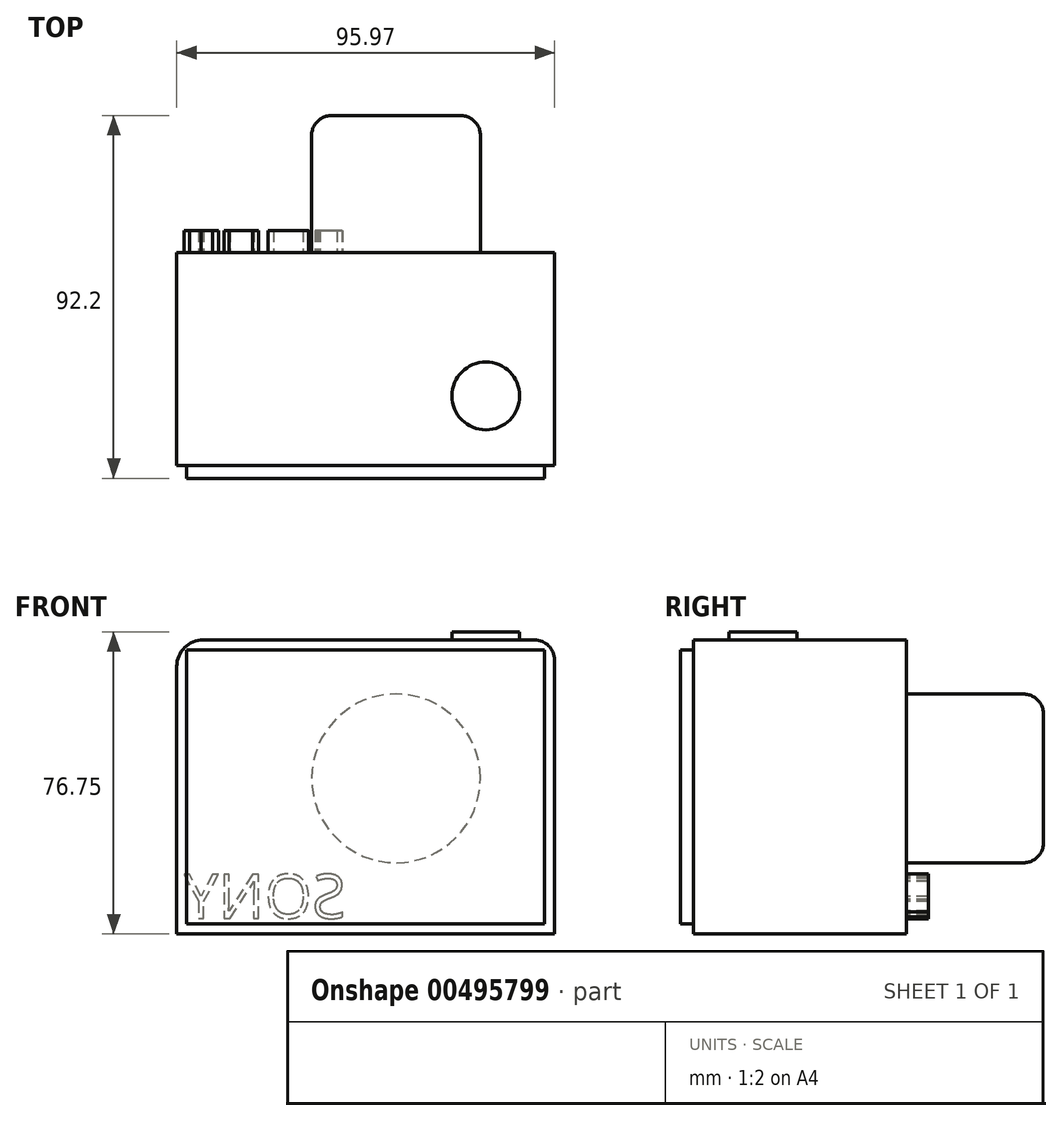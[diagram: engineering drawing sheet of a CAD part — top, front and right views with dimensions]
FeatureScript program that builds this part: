
annotation { "Feature Type Name" : "Feature", "Feature Type Description" : "" }
export const myFeature = defineFeature(function(context is Context, id is Id, definition is map)
    precondition{}
    {
        {
            var Q0;
            Q0=qCreatedBy(makeId("Front.planeOp"),FACE);
            var sketch = newSketch(context, id + "F0", { "sketchPlane" : qUnion([Q0])});
            skLineSegment(sketch, "E0.bottom", {"start": v(-64.43, 49.22) * mm, "end": v(31.54, 49.22) * mm});
            skLineSegment(sketch, "E0.top", {"start": v(-64.43, -25.49) * mm, "end": v(31.54, -25.49) * mm});
            skLineSegment(sketch, "E0.left", {"start": v(-64.43, 49.22) * mm, "end": v(-64.43, -25.49) * mm});
            skLineSegment(sketch, "E0.right", {"start": v(31.54, 49.22) * mm, "end": v(31.54, -25.49) * mm});
            skSolve(sketch);
        }
        {
            var Q0;
            Q0 = qSketchRegion(id + "F0", true);
            extrude(context, id + "F1", {"entities" : qUnion([Q0]), "depth" : 54.1 * mm});
        }
        {
            var Q0;
            Q0=makeQuery(id+"F1.opExtrude","CAP_FACE",FACE,{"disambiguationData":[OSD([sQuery(id+"F0.wireOp",EDGE,"E0.bottom"),sQuery(id+"F0.wireOp",EDGE,"E0.top"),sQuery(id+"F0.wireOp",EDGE,"E0.left"),sQuery(id+"F0.wireOp",EDGE,"E0.right")])],"isStart":false});
            shell(context, id + "F2", {"entities" : qUnion([Q0]), "thickness" : 2.54 * mm});
        }
        {
            var Q0;
            Q0=makeQuery(id+"F1.opExtrude","CAP_FACE",FACE,{"disambiguationData":[OSD([sQuery(id+"F0.wireOp",EDGE,"E0.bottom"),sQuery(id+"F0.wireOp",EDGE,"E0.top"),sQuery(id+"F0.wireOp",EDGE,"E0.left"),sQuery(id+"F0.wireOp",EDGE,"E0.right")])],"isStart":true});
            var sketch = newSketch(context, id + "F3", { "sketchPlane" : qUnion([Q0])});
            skCircle(sketch, "E1", {"center": v(8.73, 14.04) * mm, "radius": 21.44 * mm});
            skSolve(sketch);
        }
        {
            var Q0;
            Q0=makeQuery(id+"F3.imprint","IMPRINT",FACE,{"disambiguationData":[TD([[makeQuery(id+"F3.imprint","IMPRINT",EDGE,{"derivedFrom":sQuery(id+"F3.wireOp",EDGE,"E1")}),1.0]])]});
            extrude(context, id + "F4", {"entities" : qUnion([Q0]), "operationType" : NewBodyOperationType.ADD, "depth" : 34.8 * mm});
        }
        {
            var Q0;
            Q0=makeQuery(id+"F1.opExtrude","SWEPT_EDGE",EDGE,{"disambiguationData":[OSD([sQuery(id+"F0.wireOp",EDGE,"E0.bottom"),sQuery(id+"F0.wireOp",EDGE,"E0.left")])]});
            fillet(context, id + "F5", {"entities" : qUnion([Q0]), "radius" : 6.75 * mm, "tangentPropagation" : true, "allowEdgeOverflow" : false});
        }
        {
            var Q0;
            Q0=makeQuery(id+"F1.opExtrude","SWEPT_EDGE",EDGE,{"disambiguationData":[OSD([sQuery(id+"F0.wireOp",EDGE,"E0.bottom"),sQuery(id+"F0.wireOp",EDGE,"E0.right")])]});
            fillet(context, id + "F6", {"entities" : qUnion([Q0]), "radius" : 5.08 * mm, "tangentPropagation" : true, "allowEdgeOverflow" : false});
        }
        {
            var Q0;
            Q0=makeQuery(id+"F4.opExtrude","CAP_EDGE",EDGE,{"disambiguationData":[OSD([sQuery(id+"F3.wireOp",EDGE,"E1")])],"isStart":false});
            fillet(context, id + "F7", {"entities" : qUnion([Q0]), "radius" : 5.08 * mm, "tangentPropagation" : true, "allowEdgeOverflow" : false});
        }
        {
            var Q0;
            Q0=makeQuery(id+"F1.opExtrude","CAP_FACE",FACE,{"disambiguationData":[OSD([sQuery(id+"F0.wireOp",EDGE,"E0.bottom"),sQuery(id+"F0.wireOp",EDGE,"E0.top"),sQuery(id+"F0.wireOp",EDGE,"E0.left"),sQuery(id+"F0.wireOp",EDGE,"E0.right")])],"isStart":true});
            var sketch = newSketch(context, id + "F8", { "sketchPlane" : qUnion([Q0])});
            skText(sketch, "E2", { "text": "SONY", "fontName": "OpenSans-Regular.ttf"});
            const initialGuessF8  = {"E2": [0.0215, -0.02147, 1, 0, 0.0112]};
            skSetInitialGuess(sketch, initialGuessF8);
            skSolve(sketch);
        }
        {
            var Q0;
            Q0 = qSketchRegion(id + "F8", true);
            extrude(context, id + "F9", {"entities" : qUnion([Q0]), "operationType" : NewBodyOperationType.ADD, "depth" : 5.6 * mm});
        }
        {
            var Q0;
            Q0=makeQuery(id+"F1.opExtrude","SWEPT_FACE",FACE,{"disambiguationData":[OSD([sQuery(id+"F0.wireOp",EDGE,"E0.bottom")])]});
            var sketch = newSketch(context, id + "F10", { "sketchPlane" : qUnion([Q0])});
            skCircle(sketch, "E3", {"center": v(14.09, -36.44) * mm, "radius": 8.6 * mm});
            skSolve(sketch);
        }
        {
            var Q0;
            Q0=makeQuery(id+"F10.imprint","IMPRINT",FACE,{"disambiguationData":[TD([[makeQuery(id+"F10.imprint","IMPRINT",EDGE,{"derivedFrom":sQuery(id+"F10.wireOp",EDGE,"E3")}),1.0]])]});
            extrude(context, id + "F11", {"entities" : qUnion([Q0]), "operationType" : NewBodyOperationType.ADD, "depth" : 2.03 * mm});
        }
        {
            var Q0;
            Q0=makeQuery(id+"F2.opShell","OFFSET_FACE",FACE,{"disambiguationData":[OSD([sQuery(id+"F0.wireOp",EDGE,"E0.bottom"),sQuery(id+"F0.wireOp",EDGE,"E0.top"),sQuery(id+"F0.wireOp",EDGE,"E0.left"),sQuery(id+"F0.wireOp",EDGE,"E0.right")])]});
            var sketch = newSketch(context, id + "F12", { "sketchPlane" : qUnion([Q0])});
            skSolve(sketch);
        }
        {
            var Q0;
            {var subQ0=sQuery(id+"F0.wireOp",EDGE,"E0.bottom");Q0=makeQuery(id+"F12.imprint","IMPRINT",FACE,{"disambiguationData":[TD([[makeQuery(id+"F12.imprint","IMPRINT",EDGE,{"derivedFrom":makeQuery(id+"F2.opShell","OFFSET_EDGE",EDGE,{"disambiguationData":[OSD([subQ0]),TDD([makeQuery(id+"F1.opExtrude","CAP_EDGE",EDGE,{"disambiguationData":[OSD([subQ0])],"isStart":true})])]})}),-1.0]])]});}
            extrude(context, id + "F13", {"entities" : qUnion([Q0]), "operationType" : NewBodyOperationType.ADD, "depth" : 54.86 * mm});
        }
    });
